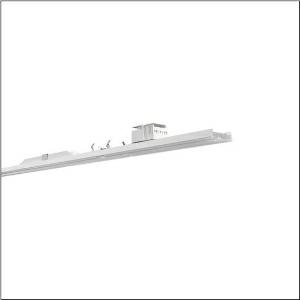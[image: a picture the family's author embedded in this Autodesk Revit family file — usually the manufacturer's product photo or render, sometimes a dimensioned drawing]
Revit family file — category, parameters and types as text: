
# Revit family: licross_r__11_recessed_mo_51tl12dv4fxf_4741
name_source: partatom
category: Lighting Fixtures
units: mm (PartAtom-declared; Revit-internal decimal feet)

## family parameters
Cut with Voids When Loaded = No
Host = Face
Light Source = No
Part Type = Normal
Room Calculation Point = No
Round Connector Dimension = Use Diameter
Shared = No

## types (1)
- --- (1 x LED, 15420 lm, 89.5 W, 4000K)
    Apparent Load = 90 VA
    CIE Flux Codes = 67 92 99 100 100
    Color Rendering = 80
    Color Temperature = 4000K
    Default Elevation = 1800 mm
    Description = Licross® 11 Recessed MOluminaire insert, length: 2.250mm, width: 66mm, height: 67mm, LED rated luminous flux: 15.420lm, light colour: 840, control gear: DALI 2, control gear: ECG DALI, with plug, 5-pole, with phase selection, mains connection: 220..240V, AC, 50/60Hz, halogen-free wiring, primary optical cover: cover, of PMMA, light emission: direct distribution, protection rating (complete): IP40, insulation class (complete): insulation class I (protective earthing), certification: CE, ENEC, VDE, protection symbol: D if used in an environment without relevant dust loads with corresponding accessories, permissible ambient temperature for indoor applications: -25..+35°C, corresponds to IFS (International Featured Standards) requirements for safety and quality in the food industry, reducing of maximum allowable ambient temperature of 5°C with ceiling mounting, packaging unit: 1 piece
    Height = 58 mm
    Lamp = 1 x LED
    Lamp Light Flux = 15420 lm
    Lamp Power = 89.5 W
    Lamp count = 1
    Length = 2250 mm
    Luminous efficacy = 172 lm/W
    Manufacturer = Siteco
    ModVariant = No
    Model = 51TL12DV4FXF
    Mounting Place = Ceiling
    Mounting Type = Pendant
    Number of Poles = 1
    OnlyDefault = Yes
    Power Factor = 1
    Product Name = Licross® 11 Recessed MO
    Product group = luminaire insert
    ProductGroupID = 902
    Protection Class = Protection class I
    Protection Degree = IP 40
    RLX_Detail_Level = 1
    RlxData = <blob elided: 26941 chars, md5=1a8dc00d>
    Socket = socket
    Standby Power = 0 W
    System Light Flux = 15420 lm
    System Power = 90 W
    Type Comments = factory setting: luminous flux: 100 % | dim-lin: 254 | 400 mA
    Type Image = l_1266722.jpg
    URL = http://relux.com
    VarID = @adj_133288
    Voltage = 0 V
    Weight = 0.00 kg
    Width = 66 mm

## geometry (parser evidence)
native form markers: Blend x4, Sweep x11
no freeform markers — native parametric forms only
